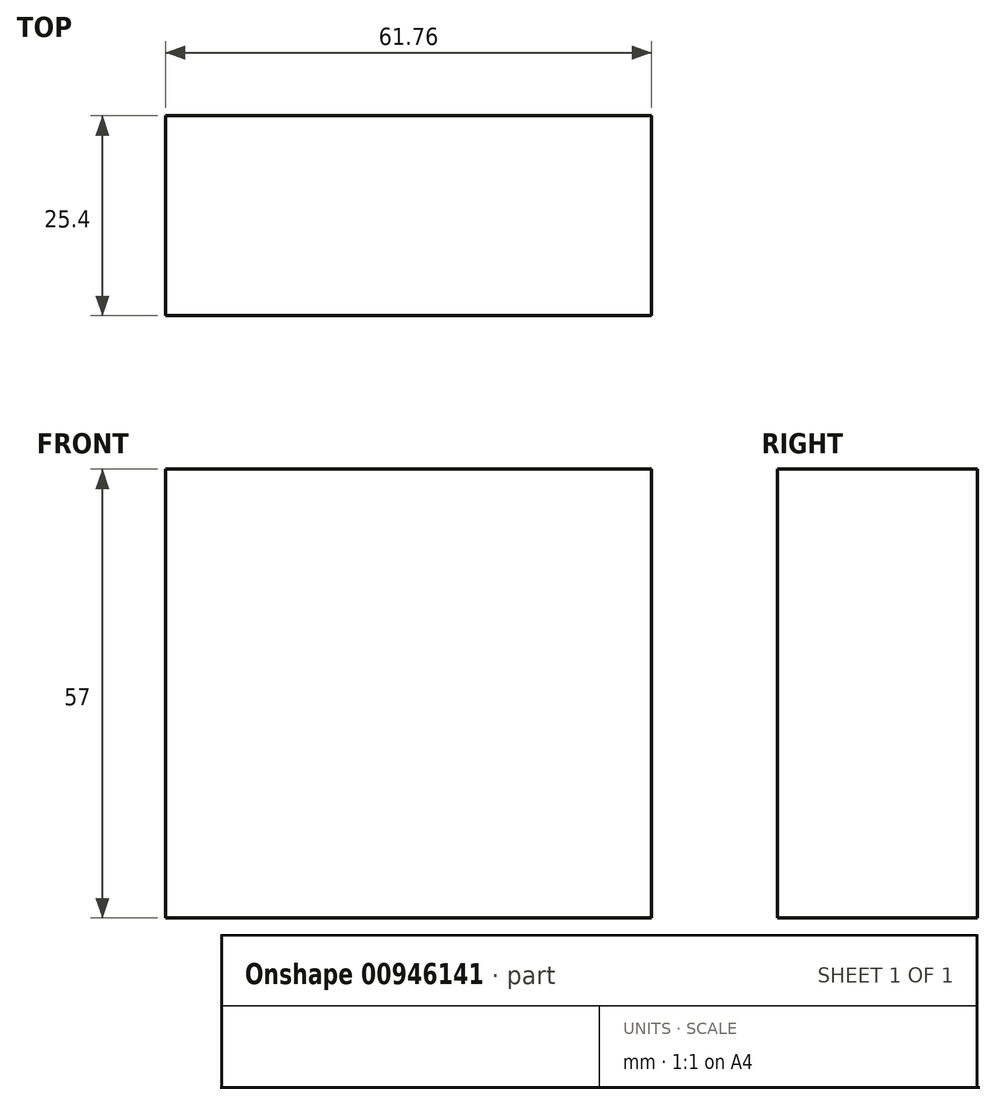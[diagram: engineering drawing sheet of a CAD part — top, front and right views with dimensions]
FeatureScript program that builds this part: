
annotation { "Feature Type Name" : "Feature", "Feature Type Description" : "" }
export const myFeature = defineFeature(function(context is Context, id is Id, definition is map)
    precondition{}
    {
        {
            var Q0;
            Q0=qCreatedBy(makeId("Front.planeOp"),FACE);
            var sketch = newSketch(context, id + "F0", { "sketchPlane" : qUnion([Q0])});
            skLineSegment(sketch, "E0.bottom", {"start": v(-103.18, 43.1) * mm, "end": v(-41.42, 43.1) * mm});
            skLineSegment(sketch, "E0.top", {"start": v(-103.18, -13.89) * mm, "end": v(-41.42, -13.89) * mm});
            skLineSegment(sketch, "E0.left", {"start": v(-103.18, 43.1) * mm, "end": v(-103.18, -13.89) * mm});
            skLineSegment(sketch, "E0.right", {"start": v(-41.42, 43.1) * mm, "end": v(-41.42, -13.89) * mm});
            skSolve(sketch);
        }
        {
            var Q0;
            Q0 = qSketchRegion(id + "F0", true);
            extrude(context, id + "F1", {"entities" : qUnion([Q0]), "depth" : 25.4 * mm, "offsetDistance" : 25.4 * mm});
        }
    });
